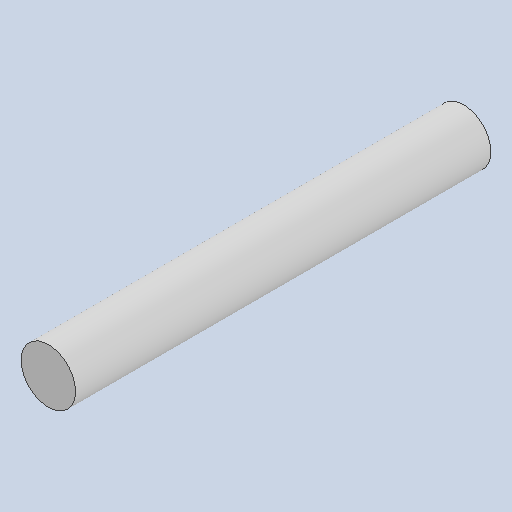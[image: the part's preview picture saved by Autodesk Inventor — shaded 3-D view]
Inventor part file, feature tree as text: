
AUTODESK INVENTOR PART (.ipt)
format: ipt  version: 2022 (Build 260153000, 153)  size: 94,720 bytes
history: native  units: mm
features: extrude x1, sketch x1
ambient origin geometry x8: Origin, YZ Plane, XZ Plane, XY Plane, X Axis, Y Axis, Z Axis, Center Point
bodies: Solid1 (feature_tree)
feature tree (2):
  extrude  "Extrusion1"  Depth=61.0mm TaperAngle=0.0deg
  sketch  "Sketch1"  dims[d0=8.0mm d1=61.0mm d2=0.0mm]
